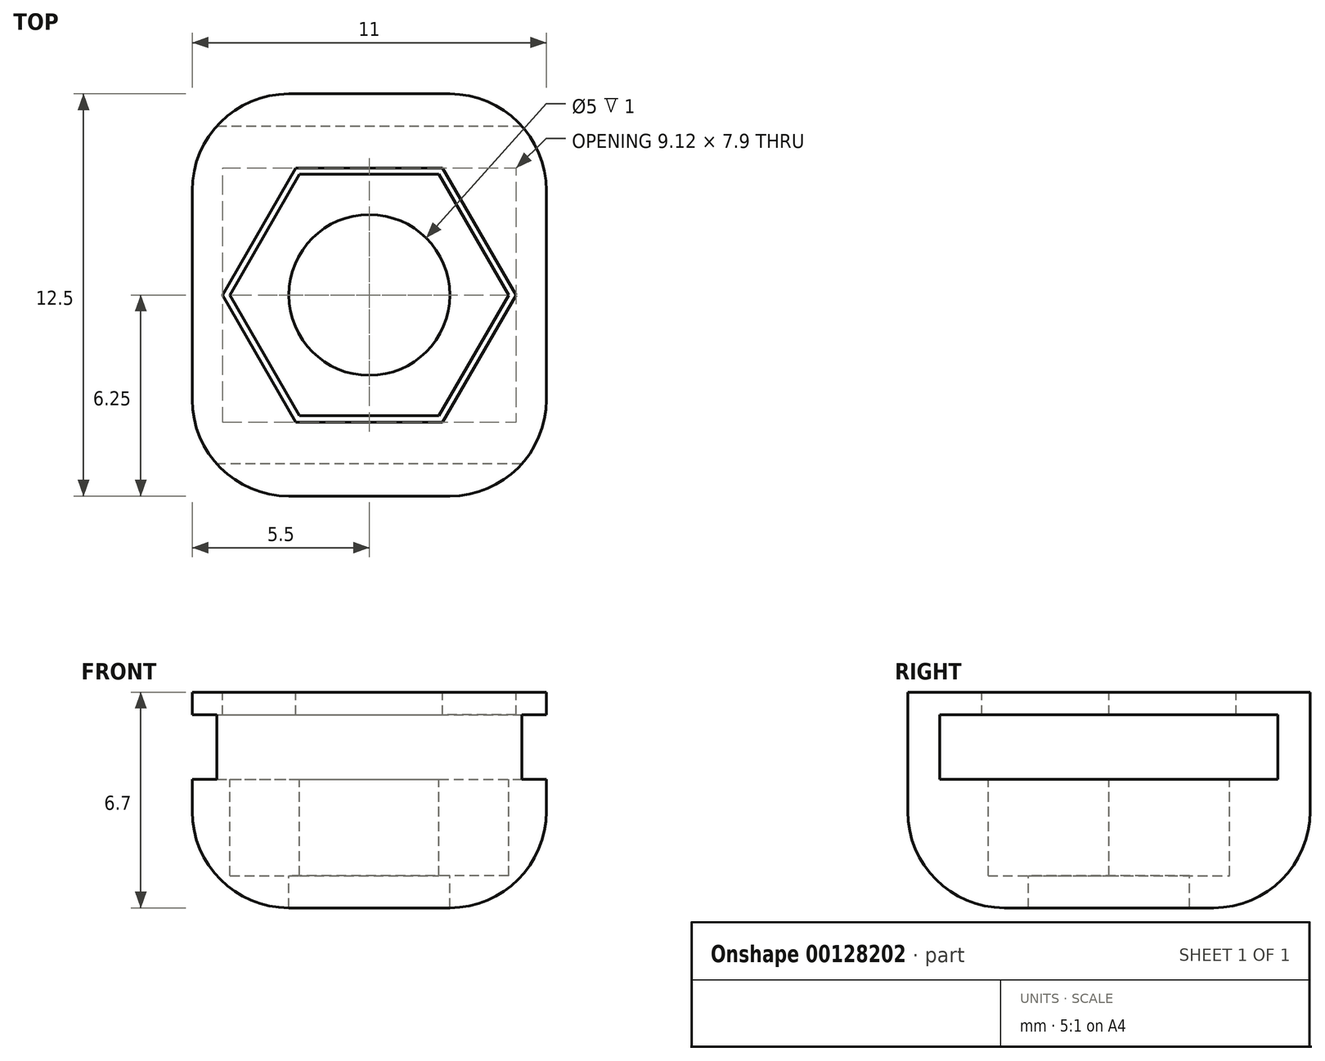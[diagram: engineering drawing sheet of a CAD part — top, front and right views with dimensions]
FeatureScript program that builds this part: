
annotation { "Feature Type Name" : "Feature", "Feature Type Description" : "" }
export const myFeature = defineFeature(function(context is Context, id is Id, definition is map)
    precondition{}
    {
        {
            var Q0;
            Q0=qCreatedBy(makeId("Top.planeOp"),FACE);
            var sketch = newSketch(context, id + "F0", { "sketchPlane" : qUnion([Q0])});
            skLineSegment(sketch, "E0.bottom", {"start": v(5.5, -6.25) * mm, "end": v(-5.5, -6.25) * mm});
            skLineSegment(sketch, "E0.top", {"start": v(5.5, 6.25) * mm, "end": v(-5.5, 6.25) * mm});
            skLineSegment(sketch, "E0.left", {"start": v(5.5, -6.25) * mm, "end": v(5.5, 6.25) * mm});
            skLineSegment(sketch, "E0.right", {"start": v(-5.5, -6.25) * mm, "end": v(-5.5, 6.25) * mm});
            skPoint(sketch, "E0.middle", {"position": v(0, 0) * mm});
            skCircle(sketch, "E1", {"center": v(0, 0) * mm, "radius": 2.5 * mm});
            skSolve(sketch);
        }
        {
            var Q0;
            Q0 = qSketchRegion(id + "F0", true);
            extrude(context, id + "F1", {"entities" : qUnion([Q0]), "oppositeDirection" : true, "depth" : 4 * mm});
        }
        {
            var Q0;
            Q0=qCreatedBy(makeId("Top.planeOp"),FACE);
            var sketch = newSketch(context, id + "F2", { "sketchPlane" : qUnion([Q0])});
            skCircle(sketch, "E2.cCircle", {"center": v(0, 0) * mm, "radius": 3.75 * mm, "construction": true});
            skLineSegment(sketch, "E2.0", {"start": v(-2.17, 3.75) * mm, "end": v(2.17, 3.75) * mm});
            skLineSegment(sketch, "E2.1", {"start": v(2.17, 3.75) * mm, "end": v(4.33, 0) * mm});
            skLineSegment(sketch, "E2.2", {"start": v(4.33, 0) * mm, "end": v(2.17, -3.75) * mm});
            skLineSegment(sketch, "E2.3", {"start": v(2.17, -3.75) * mm, "end": v(-2.17, -3.75) * mm});
            skLineSegment(sketch, "E2.4", {"start": v(-2.17, -3.75) * mm, "end": v(-4.33, 0) * mm});
            skLineSegment(sketch, "E2.5", {"start": v(-4.33, 0) * mm, "end": v(-2.17, 3.75) * mm});
            skPoint(sketch, "E2.0.midPoint", {"position": v(0, 3.75) * mm});
            skCircle(sketch, "E3", {"center": v(0, 0) * mm, "radius": 2.5 * mm});
            skSolve(sketch);
        }
        {
            var Q0;
            Q0=makeQuery(id+"F2.imprint","IMPRINT",FACE,{"disambiguationData":[TD([[makeQuery(id+"F2.imprint","IMPRINT",EDGE,{"derivedFrom":sQuery(id+"F2.wireOp",EDGE,"E2.0")}),-1.0]])]});
            extrude(context, id + "F3", {"entities" : qUnion([Q0]), "operationType" : NewBodyOperationType.REMOVE, "oppositeDirection" : true, "depth" : 3 * mm});
        }
        {
            var Q0;
            Q0=makeQuery(id+"F1.opExtrude","CAP_FACE",FACE,{"disambiguationData":[OSD([sQuery(id+"F0.wireOp",EDGE,"E0.bottom"),sQuery(id+"F0.wireOp",EDGE,"E0.top"),sQuery(id+"F0.wireOp",EDGE,"E0.left"),sQuery(id+"F0.wireOp",EDGE,"E0.right"),sQuery(id+"F0.wireOp",EDGE,"E1")])],"isStart":true});
            var sketch = newSketch(context, id + "F4", { "sketchPlane" : qUnion([Q0])});
            skLineSegment(sketch, "E4.bottom", {"start": v(-5.5, 6.25) * mm, "end": v(5.5, 6.25) * mm});
            skLineSegment(sketch, "E4.top", {"start": v(-5.5, 5.25) * mm, "end": v(5.5, 5.25) * mm});
            skLineSegment(sketch, "E4.left", {"start": v(-5.5, 6.25) * mm, "end": v(-5.5, 5.25) * mm});
            skLineSegment(sketch, "E4.right", {"start": v(5.5, 6.25) * mm, "end": v(5.5, 5.25) * mm});
            skLineSegment(sketch, "E5.bottom", {"start": v(5.5, -6.25) * mm, "end": v(-5.5, -6.25) * mm});
            skLineSegment(sketch, "E5.top", {"start": v(5.5, -5.25) * mm, "end": v(-5.5, -5.25) * mm});
            skLineSegment(sketch, "E5.left", {"start": v(5.5, -6.25) * mm, "end": v(5.5, -5.25) * mm});
            skLineSegment(sketch, "E5.right", {"start": v(-5.5, -6.25) * mm, "end": v(-5.5, -5.25) * mm});
            skSolve(sketch);
        }
        {
            var Q0;
            Q0 = qSketchRegion(id + "F4", true);
            extrude(context, id + "F5", {"entities" : qUnion([Q0]), "operationType" : NewBodyOperationType.ADD, "depth" : 2 * mm});
        }
        {
            var Q0;
            Q0=makeQuery(id+"F5.opExtrude","CAP_FACE",FACE,{"disambiguationData":[OSD([sQuery(id+"F4.wireOp",EDGE,"E5.bottom"),sQuery(id+"F4.wireOp",EDGE,"E5.top"),sQuery(id+"F4.wireOp",EDGE,"E5.left"),sQuery(id+"F4.wireOp",EDGE,"E5.right")])],"isStart":false});
            var sketch = newSketch(context, id + "F6", { "sketchPlane" : qUnion([Q0])});
            skLineSegment(sketch, "E6.bottom", {"start": v(-5.5, -6.25) * mm, "end": v(5.5, -6.25) * mm});
            skLineSegment(sketch, "E6.top", {"start": v(-5.5, 6.25) * mm, "end": v(5.5, 6.25) * mm});
            skLineSegment(sketch, "E6.left", {"start": v(-5.5, -6.25) * mm, "end": v(-5.5, 6.25) * mm});
            skLineSegment(sketch, "E6.right", {"start": v(5.5, -6.25) * mm, "end": v(5.5, 6.25) * mm});
            skSolve(sketch);
        }
        {
            var Q0;
            Q0 = qSketchRegion(id + "F6", true);
            extrude(context, id + "F7", {"entities" : qUnion([Q0]), "operationType" : NewBodyOperationType.ADD, "depth" : .7 * mm});
        }
        {
            var Q0;
            Q0=makeQuery(id+"F2.imprint","IMPRINT",FACE,{"disambiguationData":[TD([[makeQuery(id+"F2.imprint","IMPRINT",EDGE,{"derivedFrom":sQuery(id+"F2.wireOp",EDGE,"E2.0")}),-1.0]])]});
            var Q1;
            Q1=makeQuery(id+"F2.imprint","IMPRINT",FACE,{"disambiguationData":[TD([[makeQuery(id+"F2.imprint","IMPRINT",EDGE,{"derivedFrom":sQuery(id+"F2.wireOp",EDGE,"E3")}),1.0]])]});
            extrude(context, id + "F8", {"entities" : qUnion([Q0, Q1]), "operationType" : NewBodyOperationType.REMOVE, "depth" : 25 * mm});
        }
        {
            var Q0;
            Q0=makeQuery(id+"F7.boolean.opBoolean","MERGE",EDGE,{"derivedFrom":[makeQuery(id+"F5.boolean.opBoolean","MERGE",EDGE,{"derivedFrom":[makeQuery(id+"F1.opExtrude","SWEPT_EDGE",EDGE,{"disambiguationData":[OSD([sQuery(id+"F0.wireOp",EDGE,"E0.bottom"),sQuery(id+"F0.wireOp",EDGE,"E0.right")])]}),makeQuery(id+"F5.opExtrude","SWEPT_EDGE",EDGE,{"disambiguationData":[OSD([sQuery(id+"F4.wireOp",EDGE,"E5.bottom"),sQuery(id+"F4.wireOp",EDGE,"E5.right")])]})]}),makeQuery(id+"F7.opExtrude","SWEPT_EDGE",EDGE,{"disambiguationData":[OSD([sQuery(id+"F6.wireOp",EDGE,"E6.bottom"),sQuery(id+"F6.wireOp",EDGE,"E6.left")])]})]});
            var Q1;
            Q1=makeQuery(id+"F7.boolean.opBoolean","MERGE",EDGE,{"derivedFrom":[makeQuery(id+"F5.boolean.opBoolean","MERGE",EDGE,{"derivedFrom":[makeQuery(id+"F1.opExtrude","SWEPT_EDGE",EDGE,{"disambiguationData":[OSD([sQuery(id+"F0.wireOp",EDGE,"E0.bottom"),sQuery(id+"F0.wireOp",EDGE,"E0.left")])]}),makeQuery(id+"F5.opExtrude","SWEPT_EDGE",EDGE,{"disambiguationData":[OSD([sQuery(id+"F4.wireOp",EDGE,"E5.bottom"),sQuery(id+"F4.wireOp",EDGE,"E5.left")])]})]}),makeQuery(id+"F7.opExtrude","SWEPT_EDGE",EDGE,{"disambiguationData":[OSD([sQuery(id+"F6.wireOp",EDGE,"E6.bottom"),sQuery(id+"F6.wireOp",EDGE,"E6.right")])]})]});
            var Q2;
            Q2=makeQuery(id+"F7.boolean.opBoolean","MERGE",EDGE,{"derivedFrom":[makeQuery(id+"F5.boolean.opBoolean","MERGE",EDGE,{"derivedFrom":[makeQuery(id+"F1.opExtrude","SWEPT_EDGE",EDGE,{"disambiguationData":[OSD([sQuery(id+"F0.wireOp",EDGE,"E0.top"),sQuery(id+"F0.wireOp",EDGE,"E0.left")])]}),makeQuery(id+"F5.opExtrude","SWEPT_EDGE",EDGE,{"disambiguationData":[OSD([sQuery(id+"F4.wireOp",EDGE,"E4.bottom"),sQuery(id+"F4.wireOp",EDGE,"E4.right")])]})]}),makeQuery(id+"F7.opExtrude","SWEPT_EDGE",EDGE,{"disambiguationData":[OSD([sQuery(id+"F6.wireOp",EDGE,"E6.top"),sQuery(id+"F6.wireOp",EDGE,"E6.right")])]})]});
            var Q3;
            Q3=makeQuery(id+"F7.boolean.opBoolean","MERGE",EDGE,{"derivedFrom":[makeQuery(id+"F5.boolean.opBoolean","MERGE",EDGE,{"derivedFrom":[makeQuery(id+"F1.opExtrude","SWEPT_EDGE",EDGE,{"disambiguationData":[OSD([sQuery(id+"F0.wireOp",EDGE,"E0.top"),sQuery(id+"F0.wireOp",EDGE,"E0.right")])]}),makeQuery(id+"F5.opExtrude","SWEPT_EDGE",EDGE,{"disambiguationData":[OSD([sQuery(id+"F4.wireOp",EDGE,"E4.bottom"),sQuery(id+"F4.wireOp",EDGE,"E4.left")])]})]}),makeQuery(id+"F7.opExtrude","SWEPT_EDGE",EDGE,{"disambiguationData":[OSD([sQuery(id+"F6.wireOp",EDGE,"E6.top"),sQuery(id+"F6.wireOp",EDGE,"E6.left")])]})]});
            fillet(context, id + "F9", {"entities" : qUnion([Q0, Q1, Q2, Q3]), "radius" : 3 * mm, "tangentPropagation" : true, "allowEdgeOverflow" : false});
        }
        {
            var Q0;
            Q0=makeQuery(id+"F7.opExtrude","CAP_FACE",FACE,{"disambiguationData":[OSD([sQuery(id+"F6.wireOp",EDGE,"E6.bottom"),sQuery(id+"F6.wireOp",EDGE,"E6.top"),sQuery(id+"F6.wireOp",EDGE,"E6.left"),sQuery(id+"F6.wireOp",EDGE,"E6.right")])],"isStart":false});
            var sketch = newSketch(context, id + "F10", { "sketchPlane" : qUnion([Q0])});
            skCircle(sketch, "E7.cCircle", {"center": v(0, 0) * mm, "radius": 3.95 * mm, "construction": true});
            skLineSegment(sketch, "E7.0", {"start": v(-2.28, 3.95) * mm, "end": v(2.28, 3.95) * mm});
            skLineSegment(sketch, "E7.1", {"start": v(2.28, 3.95) * mm, "end": v(4.56, 0) * mm});
            skLineSegment(sketch, "E7.2", {"start": v(4.56, 0) * mm, "end": v(2.28, -3.95) * mm});
            skLineSegment(sketch, "E7.3", {"start": v(2.28, -3.95) * mm, "end": v(-2.28, -3.95) * mm});
            skLineSegment(sketch, "E7.4", {"start": v(-2.28, -3.95) * mm, "end": v(-4.56, 0) * mm});
            skLineSegment(sketch, "E7.5", {"start": v(-4.56, 0) * mm, "end": v(-2.28, 3.95) * mm});
            skPoint(sketch, "E7.0.midPoint", {"position": v(0, 3.95) * mm});
            skSolve(sketch);
        }
        {
            var Q0;
            Q0 = qSketchRegion(id + "F10", true);
            extrude(context, id + "F11", {"entities" : qUnion([Q0]), "operationType" : NewBodyOperationType.REMOVE, "oppositeDirection" : true, "depth" : 2 * mm});
        }
        {
            var Q0;
            Q0=makeQuery(id+"F1.opExtrude","CAP_EDGE",EDGE,{"disambiguationData":[OSD([sQuery(id+"F0.wireOp",EDGE,"E0.bottom")])],"isStart":false});
            fillet(context, id + "F12", {"entities" : qUnion([Q0]), "radius" : 3 * mm, "tangentPropagation" : true, "allowEdgeOverflow" : false});
        }
    });
